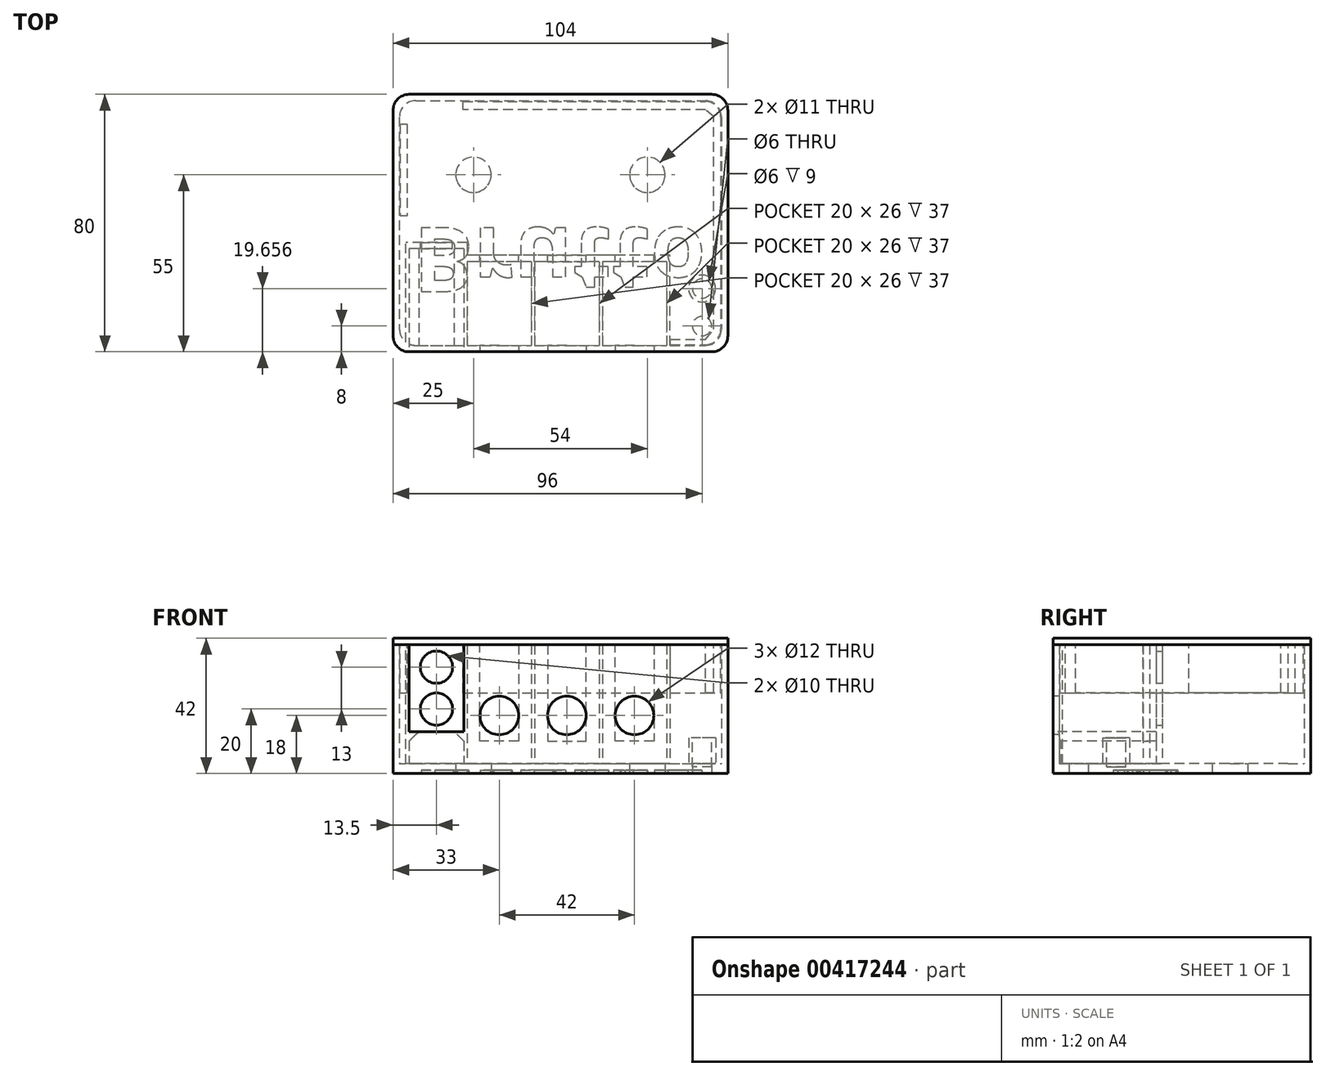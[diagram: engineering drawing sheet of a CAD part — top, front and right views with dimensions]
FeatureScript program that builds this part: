
annotation { "Feature Type Name" : "Feature", "Feature Type Description" : "" }
export const myFeature = defineFeature(function(context is Context, id is Id, definition is map)
    precondition{}
    {
        {
            var Q0;
            Q0=qCreatedBy(makeId("Top.planeOp"),FACE);
            var sketch = newSketch(context, id + "F0", { "sketchPlane" : qUnion([Q0])});
            skLineSegment(sketch, "E0.bottom", {"start": v(-50, 38) * mm, "end": v(50, 38) * mm});
            skLineSegment(sketch, "E0.top", {"start": v(-50, -38) * mm, "end": v(50, -38) * mm});
            skLineSegment(sketch, "E0.left", {"start": v(-50, 38) * mm, "end": v(-50, -38) * mm});
            skLineSegment(sketch, "E0.right", {"start": v(50, 38) * mm, "end": v(50, -38) * mm});
            skSolve(sketch);
        }
        {
            var Q0;
            Q0 = qSketchRegion(id + "F0", true);
            extrude(context, id + "F1", {"entities" : qUnion([Q0]), "depth" : 3 * mm});
        }
        {
            var Q0;
            Q0=qCreatedBy(makeId("Top.planeOp"),FACE);
            var sketch = newSketch(context, id + "F2", { "sketchPlane" : qUnion([Q0])});
            skLineSegment(sketch, "E1.top", {"start": v(-48, -38) * mm, "end": v(-47, -38) * mm});
            skLineSegment(sketch, "E2", {"start": v(-29, -38) * mm, "end": v(-29, -12) * mm});
            skLineSegment(sketch, "E3", {"start": v(-9, -38) * mm, "end": v(-9, -12) * mm});
            skLineSegment(sketch, "E4", {"start": v(-8, -38) * mm, "end": v(-8, -12) * mm});
            skLineSegment(sketch, "E5", {"start": v(12, -38) * mm, "end": v(12, -12) * mm});
            skLineSegment(sketch, "E6", {"start": v(13, -38) * mm, "end": v(13, -12) * mm});
            skLineSegment(sketch, "E7", {"start": v(33, -38) * mm, "end": v(33, -12) * mm});
            skLineSegment(sketch, "E8", {"start": v(-47, -38) * mm, "end": v(-47, -8) * mm});
            skLineSegment(sketch, "E9", {"start": v(-30, -38) * mm, "end": v(-30, -8) * mm});
            skLineSegment(sketch, "E10", {"start": v(-47, -8) * mm, "end": v(-30, -8) * mm});
            skLineSegment(sketch, "E11", {"start": v(-48, -6) * mm, "end": v(-29, -6) * mm});
            skLineSegment(sketch, "E12", {"start": v(-29, -8) * mm, "end": v(-29, -6) * mm});
            skLineSegment(sketch, "E13.trimOffspring", {"start": v(-30, -38) * mm, "end": v(-29, -38) * mm});
            skLineSegment(sketch, "E14", {"start": v(-29, -12) * mm, "end": v(-9, -12) * mm});
            skLineSegment(sketch, "E15", {"start": v(-29, -10) * mm, "end": v(34, -10) * mm});
            skLineSegment(sketch, "E16.trimOffspring", {"start": v(-8, -12) * mm, "end": v(12, -12) * mm});
            skLineSegment(sketch, "E17.trimOffspring", {"start": v(-9, -38) * mm, "end": v(-8, -38) * mm});
            skLineSegment(sketch, "E18.trimOffspring", {"start": v(13, -12) * mm, "end": v(33, -12) * mm});
            skLineSegment(sketch, "E19", {"start": v(34, -10) * mm, "end": v(34, -38) * mm});
            skLineSegment(sketch, "E20.trimOffspring", {"start": v(33, -38) * mm, "end": v(34, -38) * mm});
            skLineSegment(sketch, "E21.trimOffspring", {"start": v(12, -38) * mm, "end": v(13, -38) * mm});
            skLineSegment(sketch, "E22", {"start": v(-48, -6) * mm, "end": v(-48, -38) * mm});
            skLineSegment(sketch, "E23.trimOffspring", {"start": v(-29, -10) * mm, "end": v(-29, -8) * mm});
            skSolve(sketch);
        }
        {
            var Q0;
            Q0=makeQuery(id+"F1.opExtrude","CAP_FACE",FACE,{"disambiguationData":[OSD([sQuery(id+"F0.wireOp",EDGE,"E0.bottom"),sQuery(id+"F0.wireOp",EDGE,"E0.top"),sQuery(id+"F0.wireOp",EDGE,"E0.left"),sQuery(id+"F0.wireOp",EDGE,"E0.right")])],"isStart":true});
            var sketch = newSketch(context, id + "F3", { "sketchPlane" : qUnion([Q0])});
            skLineSegment(sketch, "E24.0", {"start": v(-50, -38) * mm, "end": v(-50, 38) * mm});
            skLineSegment(sketch, "E24.1", {"start": v(-50, -38) * mm, "end": v(50, -38) * mm});
            skLineSegment(sketch, "E24.2", {"start": v(50, -38) * mm, "end": v(50, 38) * mm});
            skLineSegment(sketch, "E24.3", {"start": v(-50, 38) * mm, "end": v(50, 38) * mm});
            skLineSegment(sketch, "E25.0", {"start": v(-52, -40) * mm, "end": v(-52, 40) * mm});
            skLineSegment(sketch, "E25.1", {"start": v(-52, -40) * mm, "end": v(52, -40) * mm});
            skLineSegment(sketch, "E25.2", {"start": v(52, -40) * mm, "end": v(52, 40) * mm});
            skLineSegment(sketch, "E25.3", {"start": v(-52, 40) * mm, "end": v(52, 40) * mm});
            skSolve(sketch);
        }
        {
            var Q0;
            Q0 = qSketchRegion(id + "F3", true);
            extrude(context, id + "F4", {"entities" : qUnion([Q0]), "operationType" : NewBodyOperationType.ADD, "oppositeDirection" : true, "depth" : 40 * mm});
        }
        {
            var Q0;
            Q0=makeQuery(id+"F4.opExtrude","SWEPT_EDGE",EDGE,{"disambiguationData":[OSD([sQuery(id+"F3.wireOp",EDGE,"E25.2"),sQuery(id+"F3.wireOp",EDGE,"E25.3")])]});
            var Q1;
            Q1=makeQuery(id+"F4.opExtrude","SWEPT_EDGE",EDGE,{"disambiguationData":[OSD([sQuery(id+"F3.wireOp",EDGE,"E25.1"),sQuery(id+"F3.wireOp",EDGE,"E25.2")])]});
            var Q2;
            Q2=makeQuery(id+"F4.opExtrude","SWEPT_EDGE",EDGE,{"disambiguationData":[OSD([sQuery(id+"F3.wireOp",EDGE,"E25.0"),sQuery(id+"F3.wireOp",EDGE,"E25.3")])]});
            var Q3;
            Q3=makeQuery(id+"F4.opExtrude","SWEPT_EDGE",EDGE,{"disambiguationData":[OSD([sQuery(id+"F3.wireOp",EDGE,"E25.0"),sQuery(id+"F3.wireOp",EDGE,"E25.1")])]});
            fillet(context, id + "F5", {"entities" : qUnion([Q0, Q1, Q2, Q3]), "radius" : 5 * mm, "tangentPropagation" : true, "allowEdgeOverflow" : false});
        }
        {
            var Q0;
            Q0=makeQuery(id+"F4.opExtrude","SWEPT_EDGE",EDGE,{"disambiguationData":[OSD([sQuery(id+"F3.wireOp",EDGE,"E24.1"),sQuery(id+"F3.wireOp",EDGE,"E24.2")])]});
            var Q1;
            Q1=makeQuery(id+"F4.opExtrude","SWEPT_EDGE",EDGE,{"disambiguationData":[OSD([sQuery(id+"F3.wireOp",EDGE,"E24.0"),sQuery(id+"F3.wireOp",EDGE,"E24.1")])]});
            var Q2;
            Q2=makeQuery(id+"F4.opExtrude","SWEPT_EDGE",EDGE,{"disambiguationData":[OSD([sQuery(id+"F3.wireOp",EDGE,"E24.0"),sQuery(id+"F3.wireOp",EDGE,"E24.3")])]});
            var Q3;
            Q3=makeQuery(id+"F4.opExtrude","SWEPT_EDGE",EDGE,{"disambiguationData":[OSD([sQuery(id+"F3.wireOp",EDGE,"E24.2"),sQuery(id+"F3.wireOp",EDGE,"E24.3")])]});
            fillet(context, id + "F6", {"entities" : qUnion([Q0, Q1, Q2, Q3]), "radius" : 5 * mm, "tangentPropagation" : true, "allowEdgeOverflow" : false});
        }
        {
            var Q0;
            Q0 = qSketchRegion(id + "F2", true);
            var Q1;
            Q1=makeQuery(id+"F4.opExtrude","CAP_FACE",FACE,{"disambiguationData":[OSD([sQuery(id+"F3.wireOp",EDGE,"E24.0"),sQuery(id+"F3.wireOp",EDGE,"E24.1"),sQuery(id+"F3.wireOp",EDGE,"E24.2"),sQuery(id+"F3.wireOp",EDGE,"E24.3"),sQuery(id+"F3.wireOp",EDGE,"E25.0"),sQuery(id+"F3.wireOp",EDGE,"E25.1"),sQuery(id+"F3.wireOp",EDGE,"E25.2"),sQuery(id+"F3.wireOp",EDGE,"E25.3")])],"isStart":false});
            extrude(context, id + "F7", {"entities" : qUnion([Q0]), "operationType" : NewBodyOperationType.ADD, "endBound" : BoundingType.UP_TO_SURFACE, "endBoundEntityFace" : qUnion([Q1]), "depth" : 25 * mm});
        }
        {
            var Q0;
            Q0=makeQuery(id+"F4.opExtrude","SWEPT_FACE",FACE,{"disambiguationData":[OSD([sQuery(id+"F3.wireOp",EDGE,"E25.3")])]});
            var sketch = newSketch(context, id + "F8", { "sketchPlane" : qUnion([Q0])});
            skCircle(sketch, "E26", {"center": v(-19, 18) * mm, "radius": 6 * mm});
            skCircle(sketch, "E27", {"center": v(2, 18) * mm, "radius": 6 * mm});
            skCircle(sketch, "E28", {"center": v(23, 18) * mm, "radius": 6 * mm});
            skLineSegment(sketch, "E29.0", {"start": v(-47, 30) * mm, "end": v(-47, 13) * mm});
            skLineSegment(sketch, "E29.3", {"start": v(-30, 30) * mm, "end": v(-30, 13) * mm});
            skPoint(sketch, "E30.orphan", {"position": v(-47, 40) * mm});
            skPoint(sketch, "E31.orphan", {"position": v(-30, 40) * mm});
            skLineSegment(sketch, "E32.bottom", {"start": v(-30, 40) * mm, "end": v(-47, 40) * mm});
            skLineSegment(sketch, "E32.top", {"start": v(-30, 13) * mm, "end": v(-47, 13) * mm});
            skLineSegment(sketch, "E32.left", {"start": v(-30, 40) * mm, "end": v(-30, 13) * mm});
            skLineSegment(sketch, "E32.right", {"start": v(-47, 40) * mm, "end": v(-47, 13) * mm});
            skPoint(sketch, "E29.2.end.orphan", {"position": v(-30, 3) * mm});
            skPoint(sketch, "E29.1.end.orphan", {"position": v(-45, 3) * mm});
            skPoint(sketch, "E33.trimOffspring.end.orphan", {"position": v(-47, 0) * mm});
            skPoint(sketch, "E33.trimOffspring.start.orphan", {"position": v(-47, 3) * mm});
            skSolve(sketch);
        }
        {
            var Q0;
            Q0 = qSketchRegion(id + "F8", true);
            extrude(context, id + "F9", {"entities" : qUnion([Q0]), "operationType" : NewBodyOperationType.REMOVE, "oppositeDirection" : true, "depth" : 14.9 * mm});
        }
        {
            var Q0;
            Q0=makeQuery(id+"F7.opExtrude","SWEPT_FACE",FACE,{"disambiguationData":[OSD([sQuery(id+"F2.wireOp",EDGE,"E15")])]});
            var sketch = newSketch(context, id + "F10", { "sketchPlane" : qUnion([Q0])});
            skLineSegment(sketch, "E34", {"start": v(-29, 40) * mm, "end": v(-29, 10) * mm});
            skLineSegment(sketch, "E35", {"start": v(-29, 10) * mm, "end": v(-17, 10) * mm});
            skLineSegment(sketch, "E36", {"start": v(-17, 10) * mm, "end": v(-17, 40) * mm});
            skLineSegment(sketch, "E37", {"start": v(-12.5, 41.57) * mm, "end": v(-12.5, -18.02) * mm, "construction": true});
            skLineSegment(sketch, "E38.MirrorCS", {"start": v(-8, 10) * mm, "end": v(-8, 40) * mm});
            skLineSegment(sketch, "E39.MirrorCS", {"start": v(4, 10) * mm, "end": v(-8, 10) * mm});
            skLineSegment(sketch, "E40.MirrorCS", {"start": v(4, 40) * mm, "end": v(4, 10) * mm});
            skLineSegment(sketch, "E41", {"start": v(-2, 44.45) * mm, "end": v(-2, -3.81) * mm, "construction": true});
            skPoint(sketch, "E41.startSnap0", {"position": v(-2, 10) * mm});
            skLineSegment(sketch, "E42.MirrorCS", {"start": v(8.5, 41.57) * mm, "end": v(8.5, -18.02) * mm, "construction": true});
            skLineSegment(sketch, "E43.MirrorCS", {"start": v(13, 40) * mm, "end": v(13, 10) * mm});
            skLineSegment(sketch, "E44.MirrorCS", {"start": v(13, 10) * mm, "end": v(25, 10) * mm});
            skLineSegment(sketch, "E45.MirrorCS", {"start": v(25, 10) * mm, "end": v(25, 40) * mm});
            skLineSegment(sketch, "E46", {"start": v(-29, 40) * mm, "end": v(-17, 40) * mm});
            skLineSegment(sketch, "E47", {"start": v(-8, 40) * mm, "end": v(4, 40) * mm});
            skLineSegment(sketch, "E48", {"start": v(13, 40) * mm, "end": v(25, 40) * mm});
            skSolve(sketch);
        }
        {
            var Q0;
            Q0 = qSketchRegion(id + "F10", true);
            extrude(context, id + "F11", {"entities" : qUnion([Q0]), "operationType" : NewBodyOperationType.REMOVE, "oppositeDirection" : true, "depth" : 7.1 * mm});
        }
        {
            var Q0;
            Q0=makeQuery(id+"F7.opExtrude","SWEPT_FACE",FACE,{"disambiguationData":[OSD([sQuery(id+"F2.wireOp",EDGE,"E11")])]});
            var sketch = newSketch(context, id + "F12", { "sketchPlane" : qUnion([Q0])});
            skPoint(sketch, "E49.orphan", {"position": v(30, 40) * mm});
            skPoint(sketch, "E50.0.end.orphan", {"position": v(30, 3) * mm});
            skPoint(sketch, "E51.orphan", {"position": v(47, 0) * mm});
            skPoint(sketch, "E52.0.end.orphan", {"position": v(47, 40) * mm});
            skLineSegment(sketch, "E53.0", {"start": v(30, 40) * mm, "end": v(30, 3) * mm});
            skLineSegment(sketch, "E54.0", {"start": v(47, 0) * mm, "end": v(47, 40) * mm});
            skLineSegment(sketch, "E55", {"start": v(30, 40) * mm, "end": v(47, 40) * mm});
            skLineSegment(sketch, "E56", {"start": v(38.5, 48.72) * mm, "end": v(38.5, -7.38) * mm, "construction": true});
            skCircle(sketch, "E57", {"center": v(38.5, 33) * mm, "radius": 5 * mm});
            skCircle(sketch, "E58", {"center": v(38.5, 20) * mm, "radius": 5 * mm});
            skSolve(sketch);
        }
        {
            var Q0;
            Q0 = qSketchRegion(id + "F12", true);
            extrude(context, id + "F13", {"entities" : qUnion([Q0]), "operationType" : NewBodyOperationType.REMOVE, "oppositeDirection" : true, "depth" : 5 * mm});
        }
        {
            var Q0;
            Q0=makeQuery(id+"F4.boolean.opBoolean","MERGE",FACE,{"derivedFrom":[makeQuery(id+"F1.opExtrude","CAP_FACE",FACE,{"disambiguationData":[OSD([sQuery(id+"F0.wireOp",EDGE,"E0.bottom"),sQuery(id+"F0.wireOp",EDGE,"E0.top"),sQuery(id+"F0.wireOp",EDGE,"E0.left"),sQuery(id+"F0.wireOp",EDGE,"E0.right")])],"isStart":true}),makeQuery(id+"F4.opExtrude","CAP_FACE",FACE,{"disambiguationData":[OSD([sQuery(id+"F3.wireOp",EDGE,"E24.0"),sQuery(id+"F3.wireOp",EDGE,"E24.1"),sQuery(id+"F3.wireOp",EDGE,"E24.2"),sQuery(id+"F3.wireOp",EDGE,"E24.3"),sQuery(id+"F3.wireOp",EDGE,"E25.0"),sQuery(id+"F3.wireOp",EDGE,"E25.1"),sQuery(id+"F3.wireOp",EDGE,"E25.2"),sQuery(id+"F3.wireOp",EDGE,"E25.3")])],"isStart":true})]});
            var sketch = newSketch(context, id + "F14", { "sketchPlane" : qUnion([Q0])});
            skCircle(sketch, "E59", {"center": v(-27, -15) * mm, "radius": 5.5 * mm});
            skCircle(sketch, "E60", {"center": v(27, -15) * mm, "radius": 5.5 * mm});
            skCircle(sketch, "E61", {"center": v(44, 32) * mm, "radius": 3 * mm});
            skSolve(sketch);
        }
        {
            var Q0;
            Q0 = qSketchRegion(id + "F14", true);
            extrude(context, id + "F15", {"entities" : qUnion([Q0]), "operationType" : NewBodyOperationType.REMOVE, "oppositeDirection" : true, "depth" : 25 * mm});
        }
        {
            var Q0;
            Q0=makeQuery(id+"F4.boolean.opBoolean","MERGE",FACE,{"derivedFrom":[makeQuery(id+"F1.opExtrude","CAP_FACE",FACE,{"disambiguationData":[OSD([sQuery(id+"F0.wireOp",EDGE,"E0.bottom"),sQuery(id+"F0.wireOp",EDGE,"E0.top"),sQuery(id+"F0.wireOp",EDGE,"E0.left"),sQuery(id+"F0.wireOp",EDGE,"E0.right")])],"isStart":true}),makeQuery(id+"F4.opExtrude","CAP_FACE",FACE,{"disambiguationData":[OSD([sQuery(id+"F3.wireOp",EDGE,"E24.0"),sQuery(id+"F3.wireOp",EDGE,"E24.1"),sQuery(id+"F3.wireOp",EDGE,"E24.2"),sQuery(id+"F3.wireOp",EDGE,"E24.3"),sQuery(id+"F3.wireOp",EDGE,"E25.0"),sQuery(id+"F3.wireOp",EDGE,"E25.1"),sQuery(id+"F3.wireOp",EDGE,"E25.2"),sQuery(id+"F3.wireOp",EDGE,"E25.3")])],"isStart":true})]});
            var sketch = newSketch(context, id + "F16", { "sketchPlane" : qUnion([Q0])});
            skText(sketch, "E62", { "text": "Brutto", "fontName": "OpenSans-Bold.ttf"});
            skPoint(sketch, "E63.2.internal.orphan", {"position": v(0, -6.97) * mm});
            skPoint(sketch, "E63.7.internal.orphan", {"position": v(42.65, -35) * mm});
            skPoint(sketch, "E64.5.internal.orphan", {"position": v(0, -18.62) * mm});
            skPoint(sketch, "E65.1.internal.orphan", {"position": v(-40.73, -28.8) * mm});
            skPoint(sketch, "E66.0.internal.orphan", {"position": v(-42.84, -28.8) * mm});
            const initialGuessF16  = {"E62": [-0.0457, 0.00148, 1, 0, 0.02]};
            skSetInitialGuess(sketch, initialGuessF16);
            skSolve(sketch);
        }
        {
            var Q0;
            Q0 = qSketchRegion(id + "F16", true);
            extrude(context, id + "F17", {"entities" : qUnion([Q0]), "operationType" : NewBodyOperationType.REMOVE, "oppositeDirection" : true, "depth" : 1 * mm});
        }
        {
            var Q0;
            Q0=makeQuery(id+"F4.opExtrude","SWEPT_FACE",FACE,{"disambiguationData":[OSD([sQuery(id+"F3.wireOp",EDGE,"E25.3")])]});
            var sketch = newSketch(context, id + "F18", { "sketchPlane" : qUnion([Q0])});
            skLineSegment(sketch, "E67", {"start": v(-47, 13) * mm, "end": v(-44, 13) * mm});
            skLineSegment(sketch, "E68", {"start": v(-44, 13) * mm, "end": v(-47, 10) * mm});
            skLineSegment(sketch, "E69", {"start": v(-47, 10) * mm, "end": v(-47, 13) * mm});
            skLineSegment(sketch, "E70", {"start": v(-30, 13) * mm, "end": v(-30, 10) * mm});
            skLineSegment(sketch, "E71", {"start": v(-30, 10) * mm, "end": v(-33, 13) * mm});
            skLineSegment(sketch, "E72", {"start": v(-33, 13) * mm, "end": v(-30, 13) * mm});
            skSolve(sketch);
        }
        {
            var Q0;
            Q0 = qSketchRegion(id + "F18", true);
            var Q1;
            Q1=makeQuery(id+"F7.opExtrude","SWEPT_FACE",FACE,{"disambiguationData":[OSD([sQuery(id+"F2.wireOp",EDGE,"E10")])]});
            extrude(context, id + "F19", {"entities" : qUnion([Q0]), "operationType" : NewBodyOperationType.ADD, "endBound" : BoundingType.UP_TO_SURFACE, "oppositeDirection" : true, "endBoundEntityFace" : qUnion([Q1]), "depth" : 25 * mm});
        }
        {
            var Q0;
            {var subQ3=sQuery(id+"F3.wireOp",EDGE,"E24.0");Q0=makeQuery(id+"F7.boolean.opBoolean","SPLIT",FACE,{"disambiguationData":[TD([makeQuery(id+"F4.opExtrude","SWEPT_FACE",FACE,{"disambiguationData":[OSD([subQ3])]})])],"derivedFrom":makeQuery(id+"F1.opExtrude","CAP_FACE",FACE,{"disambiguationData":[OSD([sQuery(id+"F0.wireOp",EDGE,"E0.bottom"),sQuery(id+"F0.wireOp",EDGE,"E0.top"),sQuery(id+"F0.wireOp",EDGE,"E0.left"),sQuery(id+"F0.wireOp",EDGE,"E0.right")])],"isStart":false})});}
            var sketch = newSketch(context, id + "F20", { "sketchPlane" : qUnion([Q0])});
            skLineSegment(sketch, "E73", {"start": v(44, -32) * mm, "end": v(44, -20.34) * mm, "construction": true});
            skLineSegment(sketch, "E74", {"start": v(44, -20.34) * mm, "end": v(44, -24.38) * mm, "construction": true});
            skCircle(sketch, "E75", {"center": v(44, -20.34) * mm, "radius": 3 * mm});
            skCircle(sketch, "E76.0", {"center": v(44, -20.34) * mm, "radius": 4.2 * mm});
            skSolve(sketch);
        }
        {
            var Q0;
            Q0=makeQuery(id+"F20.imprint","IMPRINT",FACE,{"disambiguationData":[TD([[makeQuery(id+"F20.imprint","IMPRINT",EDGE,{"derivedFrom":sQuery(id+"F20.wireOp",EDGE,"E75")}),1.0]])]});
            extrude(context, id + "F21", {"entities" : qUnion([Q0]), "operationType" : NewBodyOperationType.REMOVE, "oppositeDirection" : true, "depth" : 1 * mm});
        }
        {
            var Q0;
            Q0 = qSketchRegion(id + "F20", true);
            extrude(context, id + "F22", {"entities" : qUnion([Q0]), "operationType" : NewBodyOperationType.ADD, "depth" : 8 * mm});
        }
        {
            var Q0;
            {var subQ0=sQuery(id+"F3.wireOp",EDGE,"E25.3");var subQ1=sQuery(id+"F3.wireOp",EDGE,"E25.2");var subQ2=sQuery(id+"F3.wireOp",EDGE,"E25.1");var subQ3=sQuery(id+"F3.wireOp",EDGE,"E25.0");var subQ4=sQuery(id+"F3.wireOp",EDGE,"E24.3");var subQ5=sQuery(id+"F3.wireOp",EDGE,"E24.2");var subQ6=sQuery(id+"F3.wireOp",EDGE,"E24.1");var subQ7=sQuery(id+"F3.wireOp",EDGE,"E24.0");Q0=makeQuery(id+"F7.boolean.opBoolean","MERGE",FACE,{"derivedFrom":[makeQuery(id+"F4.opExtrude","CAP_FACE",FACE,{"disambiguationData":[OSD([subQ7,subQ6,subQ5,subQ4,subQ3,subQ2,subQ1,subQ0])],"isStart":false}),makeQuery(id+"F7.opExtrude","CAP_FACE",FACE,{"disambiguationData":[OSD([subQ7,subQ6,subQ5,subQ4,subQ3,subQ2,subQ1,subQ0])],"isStart":false})]});}
            var sketch = newSketch(context, id + "F23", { "sketchPlane" : qUnion([Q0])});
            skLineSegment(sketch, "E77.0", {"start": v(-52, 35) * mm, "end": v(-52, -35) * mm});
            skArc(sketch, "E77.1", {"start": v(-47, 40) * mm, "mid": v(-50.54, 38.54) * mm, "end": v(-52, 35) * mm});
            skLineSegment(sketch, "E77.2", {"start": v(-47, 40) * mm, "end": v(47, 40) * mm});
            skArc(sketch, "E77.3", {"start": v(52, 35) * mm, "mid": v(50.54, 38.54) * mm, "end": v(47, 40) * mm});
            skLineSegment(sketch, "E77.4", {"start": v(52, 35) * mm, "end": v(52, -35) * mm});
            skArc(sketch, "E77.5", {"start": v(47, -40) * mm, "mid": v(50.54, -38.54) * mm, "end": v(52, -35) * mm});
            skLineSegment(sketch, "E77.6", {"start": v(-30, -40) * mm, "end": v(47, -40) * mm});
            skLineSegment(sketch, "E77.7", {"start": v(-30, -40) * mm, "end": v(-47, -40) * mm});
            skArc(sketch, "E77.8", {"start": v(-52, -35) * mm, "mid": v(-50.54, -38.54) * mm, "end": v(-47, -40) * mm});
            skSolve(sketch);
        }
        {
            var Q0;
            Q0 = qSketchRegion(id + "F23", true);
            extrude(context, id + "F24", {"entities" : qUnion([Q0]), "depth" : 2 * mm});
        }
        {
            var Q0;
            Q0=makeQuery(id+"F23.imprint","IMPRINT",FACE,{"disambiguationData":[TD([[makeQuery(id+"F23.imprint","IMPRINT",EDGE,{"derivedFrom":sQuery(id+"F23.wireOp",EDGE,"E77.0")}),1.0]])]});
            var sketch = newSketch(context, id + "F25", { "sketchPlane" : qUnion([Q0])});
            skLineSegment(sketch, "E78.0", {"start": v(-50, 33) * mm, "end": v(-50, 4.43) * mm, "construction": true});
            skArc(sketch, "E78.1", {"start": v(-50, 33) * mm, "mid": v(-48.54, 36.54) * mm, "end": v(-45, 38) * mm, "construction": true});
            skArc(sketch, "E78.3", {"start": v(45, 38) * mm, "mid": v(48.54, 36.54) * mm, "end": v(50, 33) * mm, "construction": true});
            skLineSegment(sketch, "E78.4", {"start": v(50, 33) * mm, "end": v(50, -33) * mm, "construction": true});
            skArc(sketch, "E78.5", {"start": v(50, -33) * mm, "mid": v(48.54, -36.54) * mm, "end": v(45, -38) * mm, "construction": true});
            skLineSegment(sketch, "E78.6", {"start": v(34, -38) * mm, "end": v(45, -38) * mm, "construction": true});
            skLineSegment(sketch, "E78.7", {"start": v(34, -38) * mm, "end": v(34, -10) * mm, "construction": true});
            skLineSegment(sketch, "E79.0", {"start": v(-29, -6) * mm, "end": v(-29, -10) * mm, "construction": true});
            skLineSegment(sketch, "E80.0", {"start": v(34.2, -37.8) * mm, "end": v(45, -37.8) * mm});
            skLineSegment(sketch, "E80.1", {"start": v(34.2, -37.8) * mm, "end": v(34.2, -36.12) * mm});
            skLineSegment(sketch, "E81.0", {"start": v(49.8, 33) * mm, "end": v(49.8, -33) * mm});
            skLineSegment(sketch, "E81.1", {"start": v(-30.23, 37.8) * mm, "end": v(45, 37.8) * mm});
            skArc(sketch, "E82", {"start": v(45, -37.8) * mm, "mid": v(48.4, -36.4) * mm, "end": v(49.8, -33) * mm});
            skArc(sketch, "E83", {"start": v(49.8, 33) * mm, "mid": v(48.4, 36.4) * mm, "end": v(45, 37.8) * mm});
            skLineSegment(sketch, "E84", {"start": v(34.2, -36.12) * mm, "end": v(45, -36.12) * mm});
            skLineSegment(sketch, "E85", {"start": v(45, -36.12) * mm, "end": v(47.67, -33) * mm});
            skLineSegment(sketch, "E86", {"start": v(47.67, -33) * mm, "end": v(47.67, 33.02) * mm});
            skLineSegment(sketch, "E87", {"start": v(47.67, 33.02) * mm, "end": v(45, 35.26) * mm});
            skLineSegment(sketch, "E88", {"start": v(45, 35.26) * mm, "end": v(-30.23, 35.26) * mm});
            skPoint(sketch, "E78.9.start.orphan", {"position": v(-48, -37) * mm});
            skLineSegment(sketch, "E89", {"start": v(-30.23, 35.26) * mm, "end": v(-30.23, 38) * mm});
            skLineSegment(sketch, "E90.trimOffspring", {"start": v(-50, -1.5) * mm, "end": v(-50, -33) * mm, "construction": true});
            skLineSegment(sketch, "E91", {"start": v(-49.8, 30.77) * mm, "end": v(-49.8, 2.2) * mm});
            skLineSegment(sketch, "E92", {"start": v(-49.8, 2.2) * mm, "end": v(-50, 2.2) * mm});
            skLineSegment(sketch, "E93", {"start": v(-50, 30.77) * mm, "end": v(-47.63, 30.77) * mm});
            skLineSegment(sketch, "E94", {"start": v(-47.63, 30.77) * mm, "end": v(-47.63, 2.2) * mm});
            skLineSegment(sketch, "E95", {"start": v(-47.63, 2.2) * mm, "end": v(-49.8, 2.2) * mm});
            skSolve(sketch);
        }
        {
            var Q0;
            Q0 = qSketchRegion(id + "F25", true);
            extrude(context, id + "F26", {"entities" : qUnion([Q0]), "operationType" : NewBodyOperationType.ADD, "oppositeDirection" : true, "depth" : 15 * mm});
        }
    });
